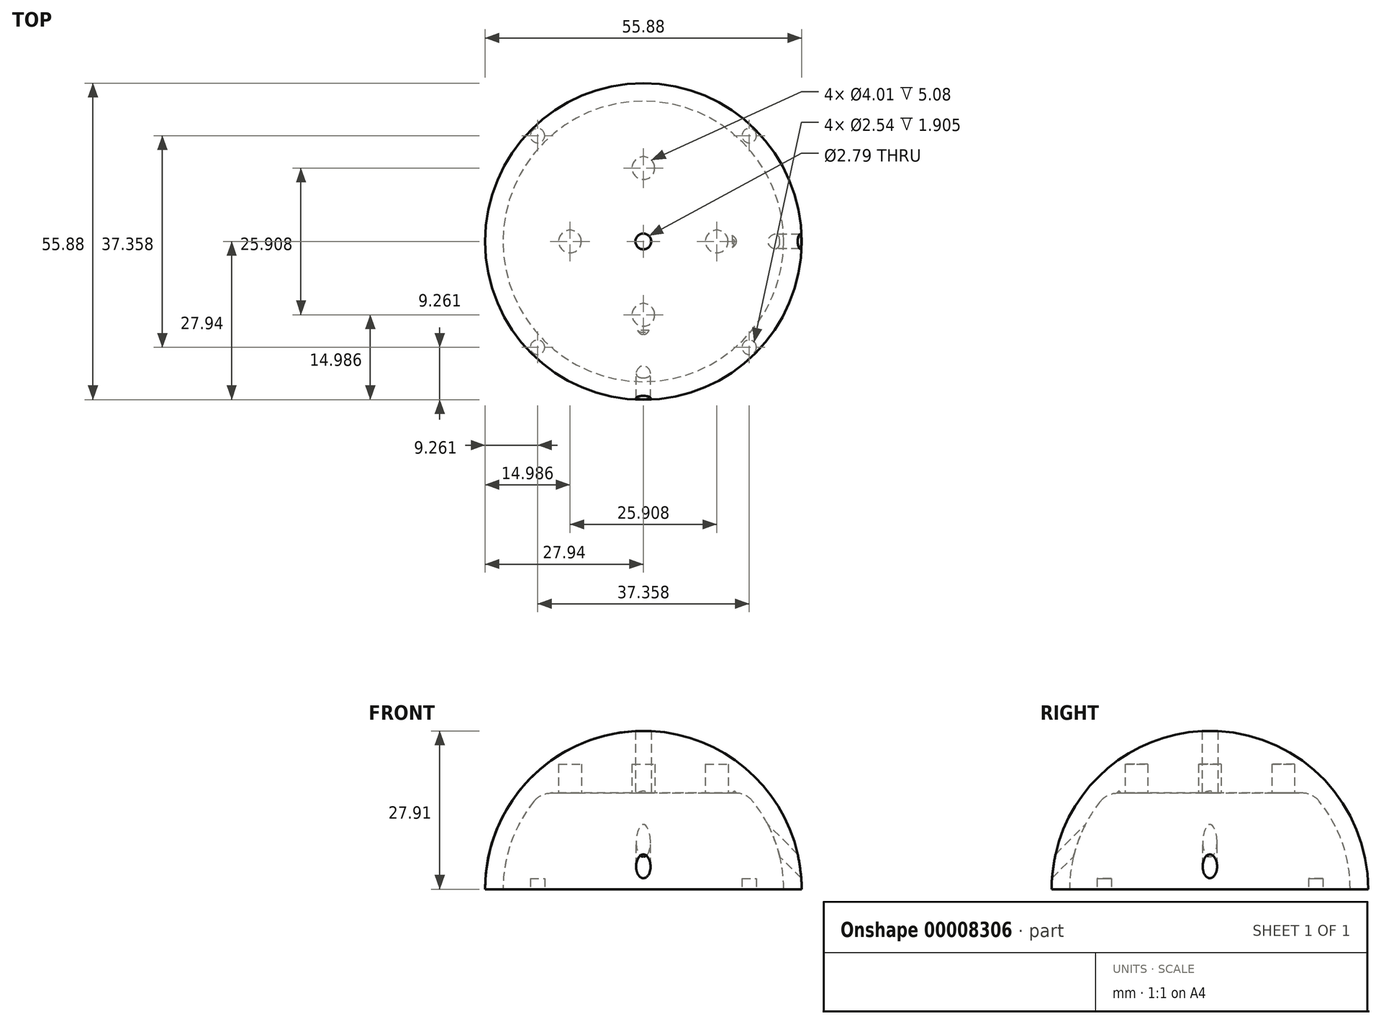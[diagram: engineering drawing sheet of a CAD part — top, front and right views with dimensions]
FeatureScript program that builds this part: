
annotation { "Feature Type Name" : "Feature", "Feature Type Description" : "" }
export const myFeature = defineFeature(function(context is Context, id is Id, definition is map)
    precondition{}
    {
        {
            var Q0;
            Q0=qCreatedBy(makeId("Front.planeOp"),FACE);
            var sketch = newSketch(context, id + "F0", { "sketchPlane" : qUnion([Q0])});
            skArc(sketch, "E0", {"start": v(27.94, 0) * mm, "mid": v(19.76, 19.76) * mm, "end": v(0, 27.94) * mm});
            skArc(sketch, "E1", {"start": v(24.77, 0) * mm, "mid": v(23.02, 9.13) * mm, "end": v(18.03, 16.97) * mm});
            skLineSegment(sketch, "E2", {"start": v(24.77, 0) * mm, "end": v(27.94, 0) * mm});
            skLineSegment(sketch, "E3", {"start": v(18.03, 16.97) * mm, "end": v(0, 16.97) * mm});
            skLineSegment(sketch, "E4", {"start": v(0, 16.97) * mm, "end": v(0, 27.94) * mm});
            skSolve(sketch);
        }
        {
            var Q0;
            Q0=makeQuery(id+"F0.imprint","IMPRINT",FACE,{"disambiguationData":[TD([[makeQuery(id+"F0.imprint","IMPRINT",EDGE,{"derivedFrom":sQuery(id+"F0.wireOp",EDGE,"E0")}),1.0]])]});
            var Q1;
            Q1=sQuery(id+"F0.wireOp",EDGE,"E4");
            revolve(context, id + "F1", {"entities" : qUnion([Q0]), "axis" : qUnion([Q1]), "revolveType" : RevolveType.FULL});
        }
        {
            var Q0;
            Q0=makeQuery(id+"F1.opRevolve","SWEPT_FACE",FACE,{"disambiguationData":[OSD([sQuery(id+"F0.wireOp",EDGE,"E3")])]});
            var sketch = newSketch(context, id + "F2", { "sketchPlane" : qUnion([Q0])});
            skCircle(sketch, "E5", {"center": v(0, 0) * mm, "radius": 1.4 * mm});
            skSolve(sketch);
        }
        {
            var Q0;
            Q0 = qSketchRegion(id + "F2", true);
            extrude(context, id + "F3", {"entities" : qUnion([Q0]), "operationType" : NewBodyOperationType.REMOVE, "endBound" : BoundingType.THROUGH_ALL, "oppositeDirection" : true, "depth" : 25.4 * mm});
        }
        {
            var Q0;
            Q0=makeQuery(id+"F1.opRevolve","SWEPT_EDGE",EDGE,{"disambiguationData":[OSD([sQuery(id+"F0.wireOp",EDGE,"E1"),sQuery(id+"F0.wireOp",EDGE,"E3")])]});
            fillet(context, id + "F4", {"entities" : qUnion([Q0]), "radius" : 3.8 * mm, "tangentPropagation" : true, "allowEdgeOverflow" : false});
        }
        {
            var Q0;
            Q0=makeQuery(id+"F1.opRevolve","SWEPT_FACE",FACE,{"disambiguationData":[OSD([sQuery(id+"F0.wireOp",EDGE,"E3")])]});
            var sketch = newSketch(context, id + "F5", { "sketchPlane" : qUnion([Q0])});
            skLineSegment(sketch, "E6.bottom", {"start": v(-4.51, 15.67) * mm, "end": v(4.51, 15.67) * mm});
            skLineSegment(sketch, "E6.top", {"start": v(-4.51, -15.67) * mm, "end": v(4.51, -15.67) * mm});
            skLineSegment(sketch, "E6.left", {"start": v(-15.67, 4.51) * mm, "end": v(-15.67, -4.51) * mm});
            skLineSegment(sketch, "E6.right", {"start": v(15.67, 4.51) * mm, "end": v(15.67, -4.51) * mm});
            skSolve(sketch);
        }
        {
            var Q0;
            Q0=sQuery(id+"F5.wireOp",EDGE,"E6.bottom");
            cPlane(context, id + "F6", {"entities" : qUnion([Q0]), "cplaneType" : CPlaneType.LINE_ANGLE, "offset" : 152.4 * mm, "angle" : 45 * degree, "width" : 152.4 * mm, "height" : 152.4 * mm});
        }
        {
            var Q0;
            Q0=qCreatedBy(id+"F6.planeOp",FACE);
            var sketch = newSketch(context, id + "F7", { "sketchPlane" : qUnion([Q0])});
            skCircle(sketch, "E7", {"center": v(0, 22.35) * mm, "radius": 1.27 * mm});
            skSolve(sketch);
        }
        {
            var Q0;
            Q0=makeQuery(id+"F7.imprint","IMPRINT",FACE,{"disambiguationData":[TD([[makeQuery(id+"F7.imprint","IMPRINT",EDGE,{"derivedFrom":sQuery(id+"F7.wireOp",EDGE,"E7")}),1.0]])]});
            extrude(context, id + "F8", {"entities" : qUnion([Q0]), "operationType" : NewBodyOperationType.REMOVE, "endBound" : BoundingType.THROUGH_ALL, "oppositeDirection" : true, "depth" : 25.4 * mm});
        }
        {
            var Q0;
            Q0=sQuery(id+"F5.wireOp",EDGE,"E6.top");
            cPlane(context, id + "F9", {"entities" : qUnion([Q0]), "cplaneType" : CPlaneType.LINE_ANGLE, "offset" : 152.4 * mm, "angle" : 315 * degree, "width" : 152.4 * mm, "height" : 152.4 * mm});
        }
        {
            var Q0;
            Q0=qCreatedBy(id+"F9.planeOp",FACE);
            var sketch = newSketch(context, id + "F10", { "sketchPlane" : qUnion([Q0])});
            skCircle(sketch, "E8", {"center": v(0, -22.35) * mm, "radius": 1.27 * mm});
            skSolve(sketch);
        }
        {
            var Q0;
            Q0 = qSketchRegion(id + "F10", true);
            extrude(context, id + "F11", {"entities" : qUnion([Q0]), "operationType" : NewBodyOperationType.REMOVE, "endBound" : BoundingType.THROUGH_ALL, "depth" : 25.4 * mm});
        }
        {
            var Q0;
            Q0=sQuery(id+"F5.wireOp",EDGE,"E6.right");
            cPlane(context, id + "F12", {"entities" : qUnion([Q0]), "cplaneType" : CPlaneType.LINE_ANGLE, "offset" : 152.4 * mm, "angle" : 315 * degree, "width" : 152.4 * mm, "height" : 152.4 * mm});
        }
        {
            var Q0;
            Q0=qCreatedBy(id+"F12.planeOp",FACE);
            var sketch = newSketch(context, id + "F13", { "sketchPlane" : qUnion([Q0])});
            skCircle(sketch, "E9", {"center": v(0, 22.35) * mm, "radius": 1.27 * mm});
            skSolve(sketch);
        }
        {
            var Q0;
            Q0 = qSketchRegion(id + "F13", true);
            extrude(context, id + "F14", {"entities" : qUnion([Q0]), "operationType" : NewBodyOperationType.REMOVE, "endBound" : BoundingType.THROUGH_ALL, "oppositeDirection" : true, "depth" : 25.4 * mm});
        }
        {
            var Q0;
            Q0=sQuery(id+"F5.wireOp",EDGE,"E6.left");
            cPlane(context, id + "F15", {"entities" : qUnion([Q0]), "cplaneType" : CPlaneType.LINE_ANGLE, "offset" : 152.4 * mm, "angle" : 45 * degree, "width" : 152.4 * mm, "height" : 152.4 * mm});
        }
        {
            var Q0;
            Q0=qCreatedBy(id+"F15.planeOp",FACE);
            var sketch = newSketch(context, id + "F16", { "sketchPlane" : qUnion([Q0])});
            skCircle(sketch, "E10", {"center": v(-22.35, 0) * mm, "radius": 1.27 * mm});
            skSolve(sketch);
        }
        {
            var Q0;
            Q0 = qSketchRegion(id + "F16", true);
            extrude(context, id + "F17", {"entities" : qUnion([Q0]), "operationType" : NewBodyOperationType.REMOVE, "endBound" : BoundingType.THROUGH_ALL, "oppositeDirection" : true, "depth" : 25.4 * mm});
        }
        {
            var Q0;
            Q0=makeQuery(id+"F1.opRevolve","SWEPT_FACE",FACE,{"disambiguationData":[OSD([sQuery(id+"F0.wireOp",EDGE,"E3")])]});
            var sketch = newSketch(context, id + "F18", { "sketchPlane" : qUnion([Q0])});
            skCircle(sketch, "E11", {"center": v(0, 12.95) * mm, "radius": 2 * mm});
            skCircle(sketch, "E12.1.0", {"center": v(-12.95, 0) * mm, "radius": 2 * mm});
            skCircle(sketch, "E12.2.0", {"center": v(0, -12.95) * mm, "radius": 2 * mm});
            skCircle(sketch, "E12.3.0", {"center": v(12.95, 0) * mm, "radius": 2 * mm});
            skPoint(sketch, "E12.center", {"position": v(0, 0) * mm});
            skSolve(sketch);
        }
        {
            var Q0;
            Q0 = qSketchRegion(id + "F18", true);
            extrude(context, id + "F19", {"entities" : qUnion([Q0]), "operationType" : NewBodyOperationType.REMOVE, "oppositeDirection" : true, "depth" : 5.08 * mm});
        }
        {
            var Q0;
            Q0=makeQuery(id+"F1.opRevolve","SWEPT_FACE",FACE,{"disambiguationData":[OSD([sQuery(id+"F0.wireOp",EDGE,"E2")])]});
            var sketch = newSketch(context, id + "F20", { "sketchPlane" : qUnion([Q0])});
            skCircle(sketch, "E13", {"center": v(-18.68, 18.68) * mm, "radius": 1.27 * mm});
            skCircle(sketch, "E14.1.0", {"center": v(18.68, 18.68) * mm, "radius": 1.27 * mm});
            skCircle(sketch, "E14.2.0", {"center": v(18.68, -18.68) * mm, "radius": 1.27 * mm});
            skPoint(sketch, "E14.center", {"position": v(0, 0) * mm});
            skLineSegment(sketch, "E14.anchor1", {"start": v(0, 0) * mm, "end": v(-18.68, 18.68) * mm, "construction": true});
            skLineSegment(sketch, "E14.anchor2", {"start": v(0, 0) * mm, "end": v(-18.68, -18.68) * mm, "construction": true});
            skCircle(sketch, "E15.1.3.0", {"center": v(-18.68, -18.68) * mm, "radius": 1.27 * mm});
            skLineSegment(sketch, "E16", {"start": v(0, 0) * mm, "end": v(0, 23.87) * mm});
            skSolve(sketch);
        }
        {
            var Q0;
            Q0 = qSketchRegion(id + "F20", true);
            extrude(context, id + "F21", {"entities" : qUnion([Q0]), "operationType" : NewBodyOperationType.REMOVE, "oppositeDirection" : true, "depth" : 1.9 * mm});
        }
    });
